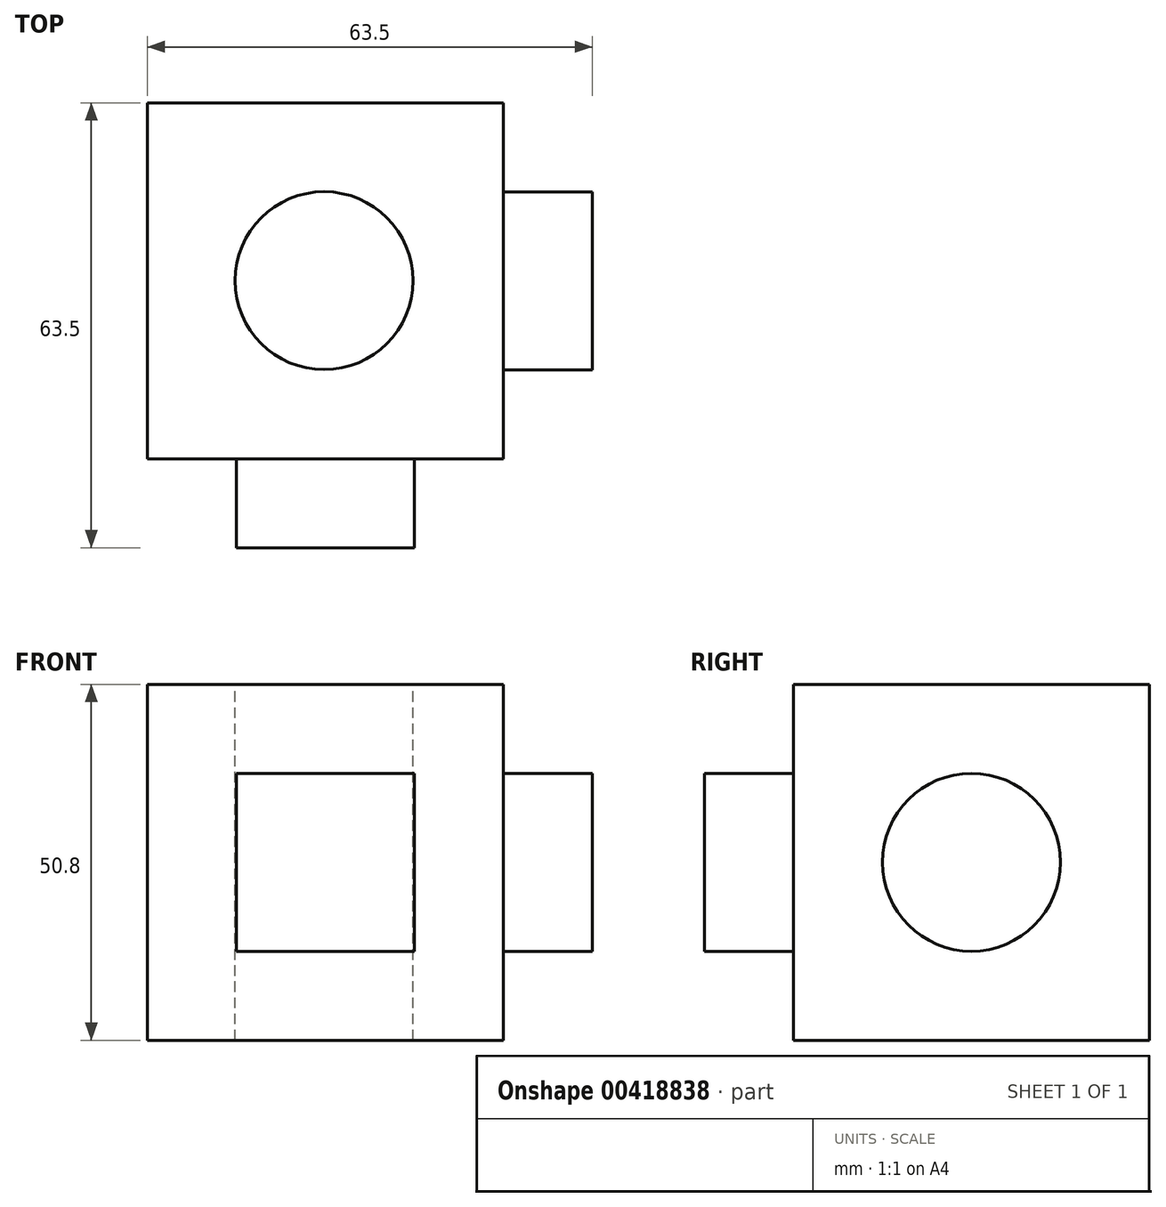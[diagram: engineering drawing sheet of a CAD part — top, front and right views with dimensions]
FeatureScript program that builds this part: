
annotation { "Feature Type Name" : "Feature", "Feature Type Description" : "" }
export const myFeature = defineFeature(function(context is Context, id is Id, definition is map)
    precondition{}
    {
        {
            var Q0;
            Q0=qCreatedBy(makeId("Front.planeOp"),FACE);
            var sketch = newSketch(context, id + "F0", { "sketchPlane" : qUnion([Q0])});
            skLineSegment(sketch, "E0.bottom", {"start": v(0, 0) * mm, "end": v(-50.8, 0) * mm});
            skLineSegment(sketch, "E0.top", {"start": v(0, 50.8) * mm, "end": v(-50.8, 50.8) * mm});
            skLineSegment(sketch, "E0.left", {"start": v(0, 0) * mm, "end": v(0, 50.8) * mm});
            skLineSegment(sketch, "E0.right", {"start": v(-50.8, 0) * mm, "end": v(-50.8, 50.8) * mm});
            skSolve(sketch);
        }
        {
            var Q0;
            Q0 = qSketchRegion(id + "F0", true);
            extrude(context, id + "F1", {"entities" : qUnion([Q0]), "depth" : 50.8 * mm});
        }
        {
            var Q0;
            Q0=makeQuery(id+"F1.opExtrude","CAP_FACE",FACE,{"disambiguationData":[OSD([sQuery(id+"F0.wireOp",EDGE,"E0.bottom"),sQuery(id+"F0.wireOp",EDGE,"E0.top"),sQuery(id+"F0.wireOp",EDGE,"E0.left"),sQuery(id+"F0.wireOp",EDGE,"E0.right")])],"isStart":false});
            var sketch = newSketch(context, id + "F2", { "sketchPlane" : qUnion([Q0])});
            skLineSegment(sketch, "E1.bottom", {"start": v(-38.1, 12.7) * mm, "end": v(-12.7, 12.7) * mm});
            skLineSegment(sketch, "E1.top", {"start": v(-38.1, 38.1) * mm, "end": v(-12.7, 38.1) * mm});
            skLineSegment(sketch, "E1.left", {"start": v(-38.1, 12.7) * mm, "end": v(-38.1, 38.1) * mm});
            skLineSegment(sketch, "E1.right", {"start": v(-12.7, 12.7) * mm, "end": v(-12.7, 38.1) * mm});
            skSolve(sketch);
        }
        {
            var Q0;
            Q0=makeQuery(id+"F2.imprint","IMPRINT",FACE,{"disambiguationData":[TD([[makeQuery(id+"F2.imprint","IMPRINT",EDGE,{"derivedFrom":sQuery(id+"F2.wireOp",EDGE,"E1.bottom")}),1.0]])]});
            extrude(context, id + "F3", {"entities" : qUnion([Q0]), "operationType" : NewBodyOperationType.ADD, "depth" : 12.7 * mm});
        }
        {
            var Q0;
            Q0=makeQuery(id+"F1.opExtrude","SWEPT_FACE",FACE,{"disambiguationData":[OSD([sQuery(id+"F0.wireOp",EDGE,"E0.left")])]});
            var sketch = newSketch(context, id + "F4", { "sketchPlane" : qUnion([Q0])});
            skCircle(sketch, "E2", {"center": v(-25.4, 25.4) * mm, "radius": 12.7 * mm});
            skSolve(sketch);
        }
        {
            var Q0;
            Q0=makeQuery(id+"F4.imprint","IMPRINT",FACE,{"disambiguationData":[TD([[makeQuery(id+"F4.imprint","IMPRINT",EDGE,{"derivedFrom":sQuery(id+"F4.wireOp",EDGE,"E2")}),1.0]])]});
            extrude(context, id + "F5", {"entities" : qUnion([Q0]), "operationType" : NewBodyOperationType.ADD, "depth" : 12.7 * mm});
        }
        {
            var Q0;
            Q0=makeQuery(id+"F1.opExtrude","SWEPT_FACE",FACE,{"disambiguationData":[OSD([sQuery(id+"F0.wireOp",EDGE,"E0.top")])]});
            var sketch = newSketch(context, id + "F6", { "sketchPlane" : qUnion([Q0])});
            skCircle(sketch, "E3", {"center": v(-25.59, -25.4) * mm, "radius": 12.7 * mm});
            skSolve(sketch);
        }
        {
            var Q0;
            Q0 = qSketchRegion(id + "F6", true);
            extrude(context, id + "F7", {"entities" : qUnion([Q0]), "operationType" : NewBodyOperationType.REMOVE, "oppositeDirection" : true, "depth" : 50.8 * mm});
        }
    });
